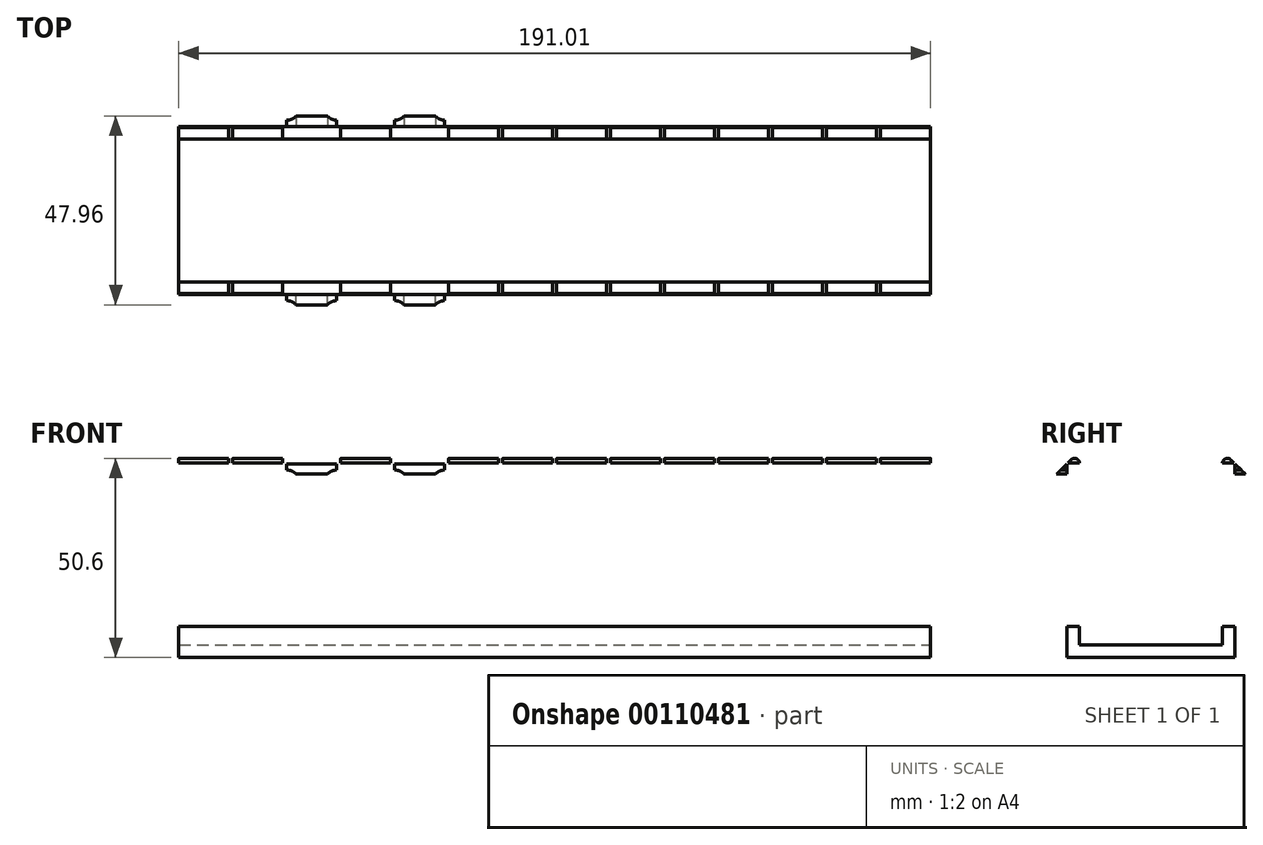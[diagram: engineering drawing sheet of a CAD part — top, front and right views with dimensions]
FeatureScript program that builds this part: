
annotation { "Feature Type Name" : "Feature", "Feature Type Description" : "" }
export const myFeature = defineFeature(function(context is Context, id is Id, definition is map)
    precondition{}
    {
        {
            var Q0;
            Q0=qCreatedBy(makeId("Right.planeOp"),FACE);
            var sketch = newSketch(context, id + "F0", { "sketchPlane" : qUnion([Q0])});
            skLineSegment(sketch, "E0.bottom", {"start": v(21.34, 1.59) * mm, "end": v(-21.34, 1.59) * mm});
            skLineSegment(sketch, "E0.top", {"start": v(21.34, -1.59) * mm, "end": v(-21.34, -1.59) * mm});
            skLineSegment(sketch, "E0.left", {"start": v(21.34, 1.59) * mm, "end": v(21.34, -1.59) * mm});
            skLineSegment(sketch, "E0.right", {"start": v(-21.34, 1.59) * mm, "end": v(-21.34, -1.59) * mm});
            skPoint(sketch, "E0.middle", {"position": v(0, 0) * mm});
            skSolve(sketch);
        }
        {
            var Q0;
            Q0 = qSketchRegion(id + "F0", true);
            extrude(context, id + "F1", {"entities" : qUnion([Q0]), "oppositeDirection" : true, "depth" : 191 * mm});
        }
        {
            var Q0;
            Q0=makeQuery(id+"F1.opExtrude","SWEPT_FACE",FACE,{"disambiguationData":[OSD([sQuery(id+"F0.wireOp",EDGE,"E0.bottom")])]});
            var sketch = newSketch(context, id + "F2", { "sketchPlane" : qUnion([Q0])});
            skLineSegment(sketch, "E1", {"start": v(-191, 18.16) * mm, "end": v(0, 18.16) * mm});
            skLineSegment(sketch, "E2", {"start": v(0, -18.16) * mm, "end": v(-191, -18.16) * mm});
            skSolve(sketch);
        }
        {
            var Q0;
            Q0 = qSketchRegion(id + "F2", true);
            var Q1;
            {var subQ0=sQuery(id+"F2.wireOp",EDGE,"E1");Q1=makeQuery(id+"F2.imprint","IMPRINT",FACE,{"disambiguationData":[TD([[makeQuery(id+"F2.imprint","IMPRINT",EDGE,{"derivedFrom":subQ0}),1.0]])]});}
            var Q2;
            {var subQ0=sQuery(id+"F2.wireOp",EDGE,"E2");Q2=makeQuery(id+"F2.imprint","IMPRINT",FACE,{"disambiguationData":[TD([[makeQuery(id+"F2.imprint","IMPRINT",EDGE,{"derivedFrom":subQ0}),1.0]])]});}
            extrude(context, id + "F3", {"entities" : qUnion([Q0, Q1, Q2]), "operationType" : NewBodyOperationType.ADD, "depth" : 4.7 * mm});
        }
        {
            var Q0;
            {var subQ0=sQuery(id+"F0.wireOp",EDGE,"E0.right");Q0=makeQuery(id+"F3.boolean.opBoolean","MERGE",FACE,{"derivedFrom":[makeQuery(id+"F1.opExtrude","SWEPT_FACE",FACE,{"disambiguationData":[OSD([subQ0])]}),makeQuery(id+"F3.opExtrude","SWEPT_FACE",FACE,{"disambiguationData":[OSD([sQuery(id+"F0.wireOp",EDGE,"E0.bottom"),subQ0])]})]});}
            var sketch = newSketch(context, id + "F4", { "sketchPlane" : qUnion([Q0])});
            skLineSegment(sketch, "E3", {"start": v(-9.53, 11.37) * mm, "end": v(-9.53, 42.86) * mm});
            skLineSegment(sketch, "E4", {"start": v(-3.18, 11.37) * mm, "end": v(-3.18, 42.86) * mm});
            skPoint(sketch, "E5.visualSharp", {"position": v(-3.18, 5.02) * mm});
            skArc(sketch, "E5.filletArc", {"start": v(-3.18, 11.37) * mm, "mid": v(-2.25, 9.12) * mm, "end": v(0, 8.2) * mm});
            skPoint(sketch, "E6.visualSharp", {"position": v(-9.53, 5.06) * mm});
            skArc(sketch, "E6.filletArc", {"start": v(-12.7, 8.2) * mm, "mid": v(-10.45, 9.12) * mm, "end": v(-9.53, 11.37) * mm});
            skArc(sketch, "E7", {"start": v(-3.18, 42.86) * mm, "mid": v(-2.25, 45.1) * mm, "end": v(0, 46.04) * mm});
            skArc(sketch, "E8", {"start": v(-9.53, 42.86) * mm, "mid": v(-10.45, 45.1) * mm, "end": v(-12.7, 46.04) * mm});
            skLineSegment(sketch, "E9", {"start": v(-12.7, 46.04) * mm, "end": v(-12.7, 49.21) * mm});
            skLineSegment(sketch, "E10", {"start": v(-12.7, 49.21) * mm, "end": v(0, 49.21) * mm});
            skLineSegment(sketch, "E11", {"start": v(0, 49.21) * mm, "end": v(0, 46.04) * mm});
            skLineSegment(sketch, "E12", {"start": v(0, 8.2) * mm, "end": v(0, 6.29) * mm});
            skLineSegment(sketch, "E13", {"start": v(-12.7, 8.2) * mm, "end": v(-12.7, 6.29) * mm});
            skLineSegment(sketch, "E14", {"start": v(-12.7, 6.29) * mm, "end": v(0, 6.29) * mm});
            skLineSegment(sketch, "E15", {"start": v(-6.35, 49.21) * mm, "end": v(-6.35, 6.29) * mm, "construction": true});
            skLineSegment(sketch, "E16.1.0.0", {"start": v(-23.24, 11.37) * mm, "end": v(-23.24, 42.86) * mm});
            skArc(sketch, "E16.1.0.1", {"start": v(-16.9, 42.86) * mm, "mid": v(-15.96, 45.1) * mm, "end": v(-13.72, 46.04) * mm});
            skArc(sketch, "E16.1.0.2", {"start": v(-26.42, 8.2) * mm, "mid": v(-24.17, 9.12) * mm, "end": v(-23.24, 11.37) * mm});
            skLineSegment(sketch, "E16.1.0.3", {"start": v(-20.07, 49.21) * mm, "end": v(-20.07, 6.29) * mm, "construction": true});
            skArc(sketch, "E16.1.0.4", {"start": v(-16.9, 11.37) * mm, "mid": v(-15.96, 9.12) * mm, "end": v(-13.72, 8.2) * mm});
            skLineSegment(sketch, "E16.1.0.5", {"start": v(-16.9, 11.37) * mm, "end": v(-16.9, 42.86) * mm});
            skArc(sketch, "E16.1.0.6", {"start": v(-23.24, 42.86) * mm, "mid": v(-24.17, 45.1) * mm, "end": v(-26.42, 46.04) * mm});
            skLineSegment(sketch, "E16.1.0.7", {"start": v(-13.72, 49.21) * mm, "end": v(-13.72, 46.04) * mm});
            skLineSegment(sketch, "E16.1.0.8", {"start": v(-26.42, 46.04) * mm, "end": v(-26.42, 49.21) * mm});
            skLineSegment(sketch, "E16.1.0.9", {"start": v(-26.42, 49.21) * mm, "end": v(-13.72, 49.21) * mm});
            skLineSegment(sketch, "E16.1.0.10", {"start": v(-26.42, 8.2) * mm, "end": v(-26.42, 6.29) * mm});
            skLineSegment(sketch, "E16.1.0.11", {"start": v(-13.72, 8.2) * mm, "end": v(-13.72, 6.29) * mm});
            skLineSegment(sketch, "E16.2.0.0", {"start": v(-36.96, 11.37) * mm, "end": v(-36.96, 42.86) * mm});
            skArc(sketch, "E16.2.0.1", {"start": v(-30.6, 42.86) * mm, "mid": v(-29.68, 45.1) * mm, "end": v(-27.43, 46.04) * mm});
            skArc(sketch, "E16.2.0.2", {"start": v(-40.13, 8.2) * mm, "mid": v(-37.89, 9.12) * mm, "end": v(-36.96, 11.37) * mm});
            skLineSegment(sketch, "E16.2.0.3", {"start": v(-33.78, 49.21) * mm, "end": v(-33.78, 6.29) * mm, "construction": true});
            skArc(sketch, "E16.2.0.4", {"start": v(-30.6, 11.37) * mm, "mid": v(-29.68, 9.12) * mm, "end": v(-27.43, 8.2) * mm});
            skLineSegment(sketch, "E16.2.0.5", {"start": v(-30.6, 11.37) * mm, "end": v(-30.6, 42.86) * mm});
            skArc(sketch, "E16.2.0.6", {"start": v(-36.96, 42.86) * mm, "mid": v(-37.89, 45.1) * mm, "end": v(-40.13, 46.04) * mm});
            skLineSegment(sketch, "E16.2.0.7", {"start": v(-27.43, 49.21) * mm, "end": v(-27.43, 46.04) * mm});
            skLineSegment(sketch, "E16.2.0.8", {"start": v(-40.13, 46.04) * mm, "end": v(-40.13, 49.21) * mm});
            skLineSegment(sketch, "E16.2.0.9", {"start": v(-40.13, 49.21) * mm, "end": v(-27.43, 49.21) * mm});
            skLineSegment(sketch, "E16.2.0.10", {"start": v(-40.13, 8.2) * mm, "end": v(-40.13, 6.29) * mm});
            skLineSegment(sketch, "E16.2.0.11", {"start": v(-27.43, 8.2) * mm, "end": v(-27.43, 6.29) * mm});
            skLineSegment(sketch, "E16.direction1", {"start": v(-12.7, 6.29) * mm, "end": v(-26.42, 6.29) * mm, "construction": true});
            skArc(sketch, "E17.1.0.0", {"start": v(-53.85, 8.2) * mm, "mid": v(-51.6, 9.12) * mm, "end": v(-50.67, 11.37) * mm});
            skLineSegment(sketch, "E17.1.0.1", {"start": v(-81.28, 46.04) * mm, "end": v(-81.28, 49.21) * mm});
            skLineSegment(sketch, "E17.1.0.2", {"start": v(-71.76, 11.37) * mm, "end": v(-71.76, 42.86) * mm});
            skArc(sketch, "E17.1.0.3", {"start": v(-58.04, 11.37) * mm, "mid": v(-57.1, 9.12) * mm, "end": v(-54.86, 8.2) * mm});
            skArc(sketch, "E17.1.0.4", {"start": v(-67.56, 8.2) * mm, "mid": v(-65.32, 9.12) * mm, "end": v(-64.39, 11.37) * mm});
            skArc(sketch, "E17.1.0.5", {"start": v(-81.28, 8.2) * mm, "mid": v(-79.03, 9.12) * mm, "end": v(-78.1, 11.37) * mm});
            skLineSegment(sketch, "E17.1.0.6", {"start": v(-78.1, 11.37) * mm, "end": v(-78.1, 42.86) * mm});
            skLineSegment(sketch, "E17.1.0.7", {"start": v(-53.85, 49.21) * mm, "end": v(-41.15, 49.21) * mm});
            skLineSegment(sketch, "E17.1.0.8", {"start": v(-41.15, 49.21) * mm, "end": v(-41.15, 46.04) * mm});
            skLineSegment(sketch, "E17.1.0.9", {"start": v(-54.86, 49.21) * mm, "end": v(-54.86, 46.04) * mm});
            skArc(sketch, "E17.1.0.10", {"start": v(-44.32, 11.37) * mm, "mid": v(-43.4, 9.12) * mm, "end": v(-41.15, 8.2) * mm});
            skArc(sketch, "E17.1.0.11", {"start": v(-71.75, 11.37) * mm, "mid": v(-70.83, 9.12) * mm, "end": v(-68.58, 8.2) * mm});
            skLineSegment(sketch, "E17.1.0.12", {"start": v(-44.32, 11.37) * mm, "end": v(-44.32, 42.86) * mm});
            skArc(sketch, "E17.1.0.13", {"start": v(-78.1, 42.86) * mm, "mid": v(-79.03, 45.1) * mm, "end": v(-81.28, 46.04) * mm});
            skArc(sketch, "E17.1.0.14", {"start": v(-44.32, 42.86) * mm, "mid": v(-43.4, 45.1) * mm, "end": v(-41.15, 46.04) * mm});
            skLineSegment(sketch, "E17.1.0.15", {"start": v(-53.85, 46.04) * mm, "end": v(-53.85, 49.21) * mm});
            skLineSegment(sketch, "E17.1.0.16", {"start": v(-68.58, 49.21) * mm, "end": v(-68.58, 46.04) * mm});
            skLineSegment(sketch, "E17.1.0.17", {"start": v(-50.67, 11.37) * mm, "end": v(-50.67, 42.86) * mm});
            skLineSegment(sketch, "E17.1.0.18", {"start": v(-64.39, 11.37) * mm, "end": v(-64.39, 42.86) * mm});
            skLineSegment(sketch, "E17.1.0.19", {"start": v(-67.56, 46.04) * mm, "end": v(-67.56, 49.21) * mm});
            skArc(sketch, "E17.1.0.20", {"start": v(-50.67, 42.86) * mm, "mid": v(-51.6, 45.1) * mm, "end": v(-53.85, 46.04) * mm});
            skLineSegment(sketch, "E17.1.0.21", {"start": v(-81.28, 49.21) * mm, "end": v(-68.58, 49.21) * mm});
            skLineSegment(sketch, "E17.1.0.22", {"start": v(-58.04, 11.37) * mm, "end": v(-58.04, 42.86) * mm});
            skArc(sketch, "E17.1.0.23", {"start": v(-71.76, 42.86) * mm, "mid": v(-70.83, 45.1) * mm, "end": v(-68.58, 46.04) * mm});
            skLineSegment(sketch, "E17.1.0.24", {"start": v(-67.56, 49.21) * mm, "end": v(-54.86, 49.21) * mm});
            skArc(sketch, "E17.1.0.25", {"start": v(-58.04, 42.86) * mm, "mid": v(-57.1, 45.1) * mm, "end": v(-54.86, 46.04) * mm});
            skArc(sketch, "E17.1.0.26", {"start": v(-64.39, 42.86) * mm, "mid": v(-65.32, 45.1) * mm, "end": v(-67.56, 46.04) * mm});
            skLineSegment(sketch, "E17.1.0.27", {"start": v(-41.15, 8.2) * mm, "end": v(-41.15, 6.29) * mm});
            skLineSegment(sketch, "E17.1.0.28", {"start": v(-53.85, 8.2) * mm, "end": v(-53.85, 6.29) * mm});
            skLineSegment(sketch, "E17.1.0.29", {"start": v(-54.86, 8.2) * mm, "end": v(-54.86, 6.29) * mm});
            skLineSegment(sketch, "E17.1.0.30", {"start": v(-67.56, 8.2) * mm, "end": v(-67.56, 6.29) * mm});
            skLineSegment(sketch, "E17.1.0.31", {"start": v(-68.58, 8.2) * mm, "end": v(-68.58, 6.29) * mm});
            skLineSegment(sketch, "E17.1.0.32", {"start": v(-81.28, 8.2) * mm, "end": v(-81.28, 6.29) * mm});
            skArc(sketch, "E17.2.0.0", {"start": v(-95, 8.2) * mm, "mid": v(-92.75, 9.12) * mm, "end": v(-91.82, 11.37) * mm});
            skLineSegment(sketch, "E17.2.0.1", {"start": v(-122.43, 46.04) * mm, "end": v(-122.43, 49.21) * mm});
            skLineSegment(sketch, "E17.2.0.2", {"start": v(-112.9, 11.37) * mm, "end": v(-112.9, 42.86) * mm});
            skArc(sketch, "E17.2.0.3", {"start": v(-99.19, 11.37) * mm, "mid": v(-98.26, 9.12) * mm, "end": v(-96.01, 8.2) * mm});
            skArc(sketch, "E17.2.0.4", {"start": v(-108.71, 8.2) * mm, "mid": v(-106.47, 9.12) * mm, "end": v(-105.54, 11.37) * mm});
            skArc(sketch, "E17.2.0.5", {"start": v(-122.43, 8.2) * mm, "mid": v(-120.18, 9.12) * mm, "end": v(-119.25, 11.37) * mm});
            skLineSegment(sketch, "E17.2.0.6", {"start": v(-119.25, 11.37) * mm, "end": v(-119.25, 42.86) * mm});
            skLineSegment(sketch, "E17.2.0.7", {"start": v(-95, 49.21) * mm, "end": v(-82.3, 49.21) * mm});
            skLineSegment(sketch, "E17.2.0.8", {"start": v(-82.3, 49.21) * mm, "end": v(-82.3, 46.04) * mm});
            skLineSegment(sketch, "E17.2.0.9", {"start": v(-96.01, 49.21) * mm, "end": v(-96.01, 46.04) * mm});
            skArc(sketch, "E17.2.0.10", {"start": v(-85.47, 11.37) * mm, "mid": v(-84.54, 9.12) * mm, "end": v(-82.3, 8.2) * mm});
            skArc(sketch, "E17.2.0.11", {"start": v(-112.9, 11.37) * mm, "mid": v(-111.97, 9.12) * mm, "end": v(-109.73, 8.2) * mm});
            skLineSegment(sketch, "E17.2.0.12", {"start": v(-85.47, 11.37) * mm, "end": v(-85.47, 42.86) * mm});
            skArc(sketch, "E17.2.0.13", {"start": v(-119.25, 42.86) * mm, "mid": v(-120.18, 45.1) * mm, "end": v(-122.43, 46.04) * mm});
            skArc(sketch, "E17.2.0.14", {"start": v(-85.47, 42.86) * mm, "mid": v(-84.54, 45.1) * mm, "end": v(-82.3, 46.04) * mm});
            skLineSegment(sketch, "E17.2.0.15", {"start": v(-95, 46.04) * mm, "end": v(-95, 49.21) * mm});
            skLineSegment(sketch, "E17.2.0.16", {"start": v(-109.73, 49.21) * mm, "end": v(-109.73, 46.04) * mm});
            skLineSegment(sketch, "E17.2.0.17", {"start": v(-91.82, 11.37) * mm, "end": v(-91.82, 42.86) * mm});
            skLineSegment(sketch, "E17.2.0.18", {"start": v(-105.54, 11.37) * mm, "end": v(-105.54, 42.86) * mm});
            skLineSegment(sketch, "E17.2.0.19", {"start": v(-108.71, 46.04) * mm, "end": v(-108.71, 49.21) * mm});
            skArc(sketch, "E17.2.0.20", {"start": v(-91.82, 42.86) * mm, "mid": v(-92.75, 45.1) * mm, "end": v(-95, 46.04) * mm});
            skLineSegment(sketch, "E17.2.0.21", {"start": v(-122.43, 49.21) * mm, "end": v(-109.73, 49.21) * mm});
            skLineSegment(sketch, "E17.2.0.22", {"start": v(-99.19, 11.37) * mm, "end": v(-99.19, 42.86) * mm});
            skArc(sketch, "E17.2.0.23", {"start": v(-112.9, 42.86) * mm, "mid": v(-111.97, 45.1) * mm, "end": v(-109.73, 46.04) * mm});
            skLineSegment(sketch, "E17.2.0.24", {"start": v(-108.71, 49.21) * mm, "end": v(-96.01, 49.21) * mm});
            skArc(sketch, "E17.2.0.25", {"start": v(-99.19, 42.86) * mm, "mid": v(-98.26, 45.1) * mm, "end": v(-96.01, 46.04) * mm});
            skArc(sketch, "E17.2.0.26", {"start": v(-105.54, 42.86) * mm, "mid": v(-106.47, 45.1) * mm, "end": v(-108.71, 46.04) * mm});
            skLineSegment(sketch, "E17.2.0.27", {"start": v(-82.3, 8.2) * mm, "end": v(-82.3, 6.29) * mm});
            skLineSegment(sketch, "E17.2.0.28", {"start": v(-95, 8.2) * mm, "end": v(-95, 6.29) * mm});
            skLineSegment(sketch, "E17.2.0.29", {"start": v(-96.01, 8.2) * mm, "end": v(-96.01, 6.29) * mm});
            skLineSegment(sketch, "E17.2.0.30", {"start": v(-108.71, 8.2) * mm, "end": v(-108.71, 6.29) * mm});
            skLineSegment(sketch, "E17.2.0.31", {"start": v(-109.73, 8.2) * mm, "end": v(-109.73, 6.29) * mm});
            skLineSegment(sketch, "E17.2.0.32", {"start": v(-122.43, 8.2) * mm, "end": v(-122.43, 6.29) * mm});
            skLineSegment(sketch, "E17.direction1", {"start": v(-40.13, 8.2) * mm, "end": v(-81.28, 8.2) * mm, "construction": true});
            skArc(sketch, "E18.1.0.0", {"start": v(-126.62, 42.86) * mm, "mid": v(-125.69, 45.1) * mm, "end": v(-123.44, 46.04) * mm});
            skLineSegment(sketch, "E18.1.0.1", {"start": v(-146.69, 11.37) * mm, "end": v(-146.69, 42.86) * mm});
            skLineSegment(sketch, "E18.1.0.2", {"start": v(-126.62, 11.37) * mm, "end": v(-126.62, 42.86) * mm});
            skArc(sketch, "E18.1.0.3", {"start": v(-136.14, 8.2) * mm, "mid": v(-133.9, 9.12) * mm, "end": v(-132.97, 11.37) * mm});
            skArc(sketch, "E18.1.0.4", {"start": v(-126.62, 11.37) * mm, "mid": v(-125.69, 9.12) * mm, "end": v(-123.44, 8.2) * mm});
            skLineSegment(sketch, "E18.1.0.5", {"start": v(-132.97, 11.37) * mm, "end": v(-132.97, 42.86) * mm});
            skLineSegment(sketch, "E18.1.0.6", {"start": v(-140.34, 11.37) * mm, "end": v(-140.34, 42.86) * mm});
            skLineSegment(sketch, "E18.1.0.7", {"start": v(-149.86, 49.21) * mm, "end": v(-137.16, 49.21) * mm});
            skLineSegment(sketch, "E18.1.0.8", {"start": v(-136.14, 49.21) * mm, "end": v(-123.44, 49.21) * mm});
            skArc(sketch, "E18.1.0.9", {"start": v(-149.86, 8.2) * mm, "mid": v(-147.61, 9.12) * mm, "end": v(-146.69, 11.37) * mm});
            skArc(sketch, "E18.1.0.10", {"start": v(-132.97, 42.86) * mm, "mid": v(-133.9, 45.1) * mm, "end": v(-136.14, 46.04) * mm});
            skArc(sketch, "E18.1.0.11", {"start": v(-140.34, 11.37) * mm, "mid": v(-139.4, 9.12) * mm, "end": v(-137.16, 8.2) * mm});
            skArc(sketch, "E18.1.0.12", {"start": v(-146.69, 42.86) * mm, "mid": v(-147.61, 45.1) * mm, "end": v(-149.86, 46.04) * mm});
            skArc(sketch, "E18.1.0.13", {"start": v(-140.34, 42.86) * mm, "mid": v(-139.4, 45.1) * mm, "end": v(-137.16, 46.04) * mm});
            skLineSegment(sketch, "E18.1.0.14", {"start": v(-123.44, 49.21) * mm, "end": v(-123.44, 46.04) * mm});
            skLineSegment(sketch, "E18.1.0.15", {"start": v(-136.14, 46.04) * mm, "end": v(-136.14, 49.21) * mm});
            skLineSegment(sketch, "E18.1.0.16", {"start": v(-149.86, 46.04) * mm, "end": v(-149.86, 49.21) * mm});
            skLineSegment(sketch, "E18.1.0.17", {"start": v(-137.16, 49.21) * mm, "end": v(-137.16, 46.04) * mm});
            skLineSegment(sketch, "E18.1.0.18", {"start": v(-136.14, 8.2) * mm, "end": v(-136.14, 6.29) * mm});
            skLineSegment(sketch, "E18.1.0.19", {"start": v(-137.16, 8.2) * mm, "end": v(-137.16, 6.29) * mm});
            skLineSegment(sketch, "E18.1.0.20", {"start": v(-149.86, 8.2) * mm, "end": v(-149.86, 6.29) * mm});
            skLineSegment(sketch, "E18.1.0.21", {"start": v(-123.44, 8.2) * mm, "end": v(-123.44, 6.29) * mm});
            skArc(sketch, "E18.2.0.0", {"start": v(-154.05, 42.86) * mm, "mid": v(-153.12, 45.1) * mm, "end": v(-150.88, 46.04) * mm});
            skLineSegment(sketch, "E18.2.0.1", {"start": v(-174.12, 11.37) * mm, "end": v(-174.12, 42.86) * mm});
            skLineSegment(sketch, "E18.2.0.2", {"start": v(-154.05, 11.37) * mm, "end": v(-154.05, 42.86) * mm});
            skArc(sketch, "E18.2.0.3", {"start": v(-163.58, 8.2) * mm, "mid": v(-161.33, 9.12) * mm, "end": v(-160.4, 11.37) * mm});
            skArc(sketch, "E18.2.0.4", {"start": v(-154.05, 11.37) * mm, "mid": v(-153.12, 9.12) * mm, "end": v(-150.88, 8.2) * mm});
            skLineSegment(sketch, "E18.2.0.5", {"start": v(-160.4, 11.37) * mm, "end": v(-160.4, 42.86) * mm});
            skLineSegment(sketch, "E18.2.0.6", {"start": v(-167.77, 11.37) * mm, "end": v(-167.77, 42.86) * mm});
            skLineSegment(sketch, "E18.2.0.7", {"start": v(-177.3, 49.21) * mm, "end": v(-164.6, 49.21) * mm});
            skLineSegment(sketch, "E18.2.0.8", {"start": v(-163.58, 49.21) * mm, "end": v(-150.88, 49.21) * mm});
            skArc(sketch, "E18.2.0.9", {"start": v(-177.3, 8.2) * mm, "mid": v(-175.05, 9.12) * mm, "end": v(-174.12, 11.37) * mm});
            skArc(sketch, "E18.2.0.10", {"start": v(-160.4, 42.86) * mm, "mid": v(-161.33, 45.1) * mm, "end": v(-163.58, 46.04) * mm});
            skArc(sketch, "E18.2.0.11", {"start": v(-167.77, 11.37) * mm, "mid": v(-166.84, 9.12) * mm, "end": v(-164.6, 8.2) * mm});
            skArc(sketch, "E18.2.0.12", {"start": v(-174.12, 42.86) * mm, "mid": v(-175.05, 45.1) * mm, "end": v(-177.3, 46.04) * mm});
            skArc(sketch, "E18.2.0.13", {"start": v(-167.77, 42.86) * mm, "mid": v(-166.84, 45.1) * mm, "end": v(-164.6, 46.04) * mm});
            skLineSegment(sketch, "E18.2.0.14", {"start": v(-150.88, 49.21) * mm, "end": v(-150.88, 46.04) * mm});
            skLineSegment(sketch, "E18.2.0.15", {"start": v(-163.58, 46.04) * mm, "end": v(-163.58, 49.21) * mm});
            skLineSegment(sketch, "E18.2.0.16", {"start": v(-177.3, 46.04) * mm, "end": v(-177.3, 49.21) * mm});
            skLineSegment(sketch, "E18.2.0.17", {"start": v(-164.6, 49.21) * mm, "end": v(-164.6, 46.04) * mm});
            skLineSegment(sketch, "E18.2.0.18", {"start": v(-163.58, 8.2) * mm, "end": v(-163.58, 6.29) * mm});
            skLineSegment(sketch, "E18.2.0.19", {"start": v(-164.6, 8.2) * mm, "end": v(-164.6, 6.29) * mm});
            skLineSegment(sketch, "E18.2.0.20", {"start": v(-177.3, 8.2) * mm, "end": v(-177.3, 6.29) * mm});
            skLineSegment(sketch, "E18.2.0.21", {"start": v(-150.88, 8.2) * mm, "end": v(-150.88, 6.29) * mm});
            skLineSegment(sketch, "E18.direction1", {"start": v(-122.43, 8.2) * mm, "end": v(-149.86, 8.2) * mm, "construction": true});
            skArc(sketch, "E19.1.0.0", {"start": v(-191, 8.2) * mm, "mid": v(-188.76, 9.12) * mm, "end": v(-187.83, 11.37) * mm});
            skLineSegment(sketch, "E19.1.0.1", {"start": v(-191, 49.21) * mm, "end": v(-178.3, 49.21) * mm});
            skLineSegment(sketch, "E19.1.0.2", {"start": v(-181.48, 11.37) * mm, "end": v(-181.48, 42.86) * mm});
            skArc(sketch, "E19.1.0.3", {"start": v(-187.83, 42.86) * mm, "mid": v(-188.76, 45.1) * mm, "end": v(-191, 46.04) * mm});
            skArc(sketch, "E19.1.0.4", {"start": v(-181.48, 11.37) * mm, "mid": v(-180.55, 9.12) * mm, "end": v(-178.3, 8.2) * mm});
            skLineSegment(sketch, "E19.1.0.5", {"start": v(-187.83, 11.37) * mm, "end": v(-187.83, 42.86) * mm});
            skArc(sketch, "E19.1.0.6", {"start": v(-181.48, 42.86) * mm, "mid": v(-180.55, 45.1) * mm, "end": v(-178.3, 46.04) * mm});
            skLineSegment(sketch, "E19.1.0.7", {"start": v(-178.3, 49.21) * mm, "end": v(-178.3, 46.04) * mm});
            skLineSegment(sketch, "E19.1.0.8", {"start": v(-191, 46.04) * mm, "end": v(-191, 49.21) * mm});
            skLineSegment(sketch, "E19.1.0.9", {"start": v(-178.3, 8.2) * mm, "end": v(-178.3, 6.29) * mm});
            skLineSegment(sketch, "E19.1.0.10", {"start": v(-191, 8.2) * mm, "end": v(-191, 6.29) * mm});
            skLineSegment(sketch, "E19.direction1", {"start": v(-177.3, 6.29) * mm, "end": v(-191, 6.29) * mm, "construction": true});
            skSolve(sketch);
        }
        {
            var Q0;
            Q0 = qSketchRegion(id + "F4", true);
            var Q1;
            Q1=makeQuery(id+"F4.imprint","IMPRINT",FACE,{"disambiguationData":[TD([[makeQuery(id+"F4.imprint","IMPRINT",EDGE,{"derivedFrom":sQuery(id+"F4.wireOp",EDGE,"E16.1.0.0")}),-1.0]])]});
            var Q2;
            Q2=makeQuery(id+"F4.imprint","IMPRINT",FACE,{"disambiguationData":[TD([[makeQuery(id+"F4.imprint","IMPRINT",EDGE,{"derivedFrom":sQuery(id+"F4.wireOp",EDGE,"E16.2.0.0")}),-1.0]])]});
            var Q3;
            Q3=makeQuery(id+"F4.imprint","IMPRINT",FACE,{"disambiguationData":[TD([[makeQuery(id+"F4.imprint","IMPRINT",EDGE,{"derivedFrom":sQuery(id+"F4.wireOp",EDGE,"E17.1.0.0")}),-1.0]])]});
            var Q4;
            Q4=makeQuery(id+"F4.imprint","IMPRINT",FACE,{"disambiguationData":[TD([[makeQuery(id+"F4.imprint","IMPRINT",EDGE,{"derivedFrom":sQuery(id+"F4.wireOp",EDGE,"E17.1.0.3")}),-1.0]])]});
            var Q5;
            Q5=makeQuery(id+"F4.imprint","IMPRINT",FACE,{"disambiguationData":[TD([[makeQuery(id+"F4.imprint","IMPRINT",EDGE,{"derivedFrom":sQuery(id+"F4.wireOp",EDGE,"E17.1.0.1")}),-1.0]])]});
            var Q6;
            Q6=makeQuery(id+"F4.imprint","IMPRINT",FACE,{"disambiguationData":[TD([[makeQuery(id+"F4.imprint","IMPRINT",EDGE,{"derivedFrom":sQuery(id+"F4.wireOp",EDGE,"E17.2.0.0")}),-1.0]])]});
            var Q7;
            Q7=makeQuery(id+"F4.imprint","IMPRINT",FACE,{"disambiguationData":[TD([[makeQuery(id+"F4.imprint","IMPRINT",EDGE,{"derivedFrom":sQuery(id+"F4.wireOp",EDGE,"E17.2.0.3")}),-1.0]])]});
            var Q8;
            Q8=makeQuery(id+"F4.imprint","IMPRINT",FACE,{"disambiguationData":[TD([[makeQuery(id+"F4.imprint","IMPRINT",EDGE,{"derivedFrom":sQuery(id+"F4.wireOp",EDGE,"E17.2.0.1")}),-1.0]])]});
            var Q9;
            Q9=makeQuery(id+"F4.imprint","IMPRINT",FACE,{"disambiguationData":[TD([[makeQuery(id+"F4.imprint","IMPRINT",EDGE,{"derivedFrom":sQuery(id+"F4.wireOp",EDGE,"E18.1.0.0")}),1.0]])]});
            var Q10;
            Q10=makeQuery(id+"F4.imprint","IMPRINT",FACE,{"disambiguationData":[TD([[makeQuery(id+"F4.imprint","IMPRINT",EDGE,{"derivedFrom":sQuery(id+"F4.wireOp",EDGE,"E18.1.0.1")}),-1.0]])]});
            var Q11;
            Q11=makeQuery(id+"F4.imprint","IMPRINT",FACE,{"disambiguationData":[TD([[makeQuery(id+"F4.imprint","IMPRINT",EDGE,{"derivedFrom":sQuery(id+"F4.wireOp",EDGE,"E18.2.0.0")}),1.0]])]});
            var Q12;
            Q12=makeQuery(id+"F4.imprint","IMPRINT",FACE,{"disambiguationData":[TD([[makeQuery(id+"F4.imprint","IMPRINT",EDGE,{"derivedFrom":sQuery(id+"F4.wireOp",EDGE,"E18.2.0.1")}),-1.0]])]});
            var Q13;
            Q13=makeQuery(id+"F4.imprint","IMPRINT",FACE,{"disambiguationData":[TD([[makeQuery(id+"F4.imprint","IMPRINT",EDGE,{"derivedFrom":sQuery(id+"F4.wireOp",EDGE,"E19.1.0.0")}),-1.0]])]});
            extrude(context, id + "F5", {"entities" : qUnion([Q0, Q1, Q2, Q3, Q4, Q5, Q6, Q7, Q8, Q9, Q10, Q11, Q12, Q13]), "operationType" : NewBodyOperationType.ADD, "oppositeDirection" : true, "depth" : 3.17 * mm});
        }
        {
            var Q0;
            Q0=makeQuery(id+"F5.opExtrude","SWEPT_FACE",FACE,{"disambiguationData":[OSD([sQuery(id+"F4.wireOp",EDGE,"E11")])]});
            var sketch = newSketch(context, id + "F6", { "sketchPlane" : qUnion([Q0])});
            skLineSegment(sketch, "E20", {"start": v(-23.98, 44.98) * mm, "end": v(-21.34, 44.98) * mm});
            skArc(sketch, "E21", {"start": v(-20.32, 48.64) * mm, "mid": v(-18.89, 48.89) * mm, "end": v(-18.16, 47.62) * mm});
            skLineSegment(sketch, "E22", {"start": v(-23.98, 44.98) * mm, "end": v(-20.32, 48.64) * mm});
            skLineSegment(sketch, "E23", {"start": v(-21.34, 44.98) * mm, "end": v(-21.34, 47.62) * mm});
            skLineSegment(sketch, "E24", {"start": v(-21.34, 47.62) * mm, "end": v(-18.16, 47.62) * mm});
            skSolve(sketch);
        }
        {
            var Q0;
            {var subQ0=sQuery(id+"F6.wireOp",EDGE,"E20");Q0=makeQuery(id+"F6.imprint","IMPRINT",FACE,{"disambiguationData":[TD([[makeQuery(id+"F6.imprint","IMPRINT",EDGE,{"derivedFrom":subQ0}),1.0]])]});}
            extrude(context, id + "F7", {"entities" : qUnion([Q0]), "operationType" : NewBodyOperationType.ADD, "oppositeDirection" : true, "depth" : 191 * mm});
        }
        {
            var Q0;
            {var subQ0=sQuery(id+"F4.wireOp",EDGE,"E11");var subQ1=makeQuery(id+"F5.opExtrude","SWEPT_EDGE",EDGE,{"disambiguationData":[OSD([sQuery(id+"F4.wireOp",EDGE,"E10"),subQ0])]});Q0=makeQuery(id+"F6.imprint","IMPRINT",FACE,{"disambiguationData":[TD([[makeQuery(id+"F6.imprint","IMPRINT",EDGE,{"derivedFrom":subQ1}),1.0]])]});}
            extrude(context, id + "F8", {"entities" : qUnion([Q0]), "operationType" : NewBodyOperationType.REMOVE, "endBound" : BoundingType.THROUGH_ALL, "oppositeDirection" : true, "depth" : 25.4 * mm});
        }
        {
            var Q0;
            Q0=makeQuery(id+"F5.boolean.opBoolean","MERGE",FACE,{"derivedFrom":[makeQuery(id+"F3.opExtrude","SWEPT_FACE",FACE,{"disambiguationData":[OSD([sQuery(id+"F2.wireOp",EDGE,"E2")])]}),makeQuery(id+"F5.opExtrude","CAP_FACE",FACE,{"disambiguationData":[OSD([sQuery(id+"F4.wireOp",EDGE,"E3"),sQuery(id+"F4.wireOp",EDGE,"E4"),sQuery(id+"F4.wireOp",EDGE,"E5.filletArc"),sQuery(id+"F4.wireOp",EDGE,"E6.filletArc"),sQuery(id+"F4.wireOp",EDGE,"E7"),sQuery(id+"F4.wireOp",EDGE,"E8"),sQuery(id+"F4.wireOp",EDGE,"E9"),sQuery(id+"F4.wireOp",EDGE,"E10"),sQuery(id+"F4.wireOp",EDGE,"E11"),sQuery(id+"F4.wireOp",EDGE,"E12"),sQuery(id+"F4.wireOp",EDGE,"E13"),sQuery(id+"F4.wireOp",EDGE,"E14")])],"isStart":false})]});
            var sketch = newSketch(context, id + "F9", { "sketchPlane" : qUnion([Q0])});
            skArc(sketch, "E25.0", {"start": v(3.18, 42.86) * mm, "mid": v(2.25, 45.1) * mm, "end": v(0, 46.04) * mm});
            skArc(sketch, "E26.0", {"start": v(9.53, 42.86) * mm, "mid": v(10.45, 45.1) * mm, "end": v(12.7, 46.04) * mm});
            skLineSegment(sketch, "E27", {"start": v(0, 46.04) * mm, "end": v(0, 42.86) * mm});
            skLineSegment(sketch, "E28", {"start": v(0, 42.86) * mm, "end": v(3.18, 42.86) * mm});
            skLineSegment(sketch, "E29", {"start": v(9.53, 42.86) * mm, "end": v(12.7, 42.86) * mm});
            skLineSegment(sketch, "E30", {"start": v(12.7, 46.04) * mm, "end": v(12.7, 42.86) * mm});
            skSolve(sketch);
        }
        {
            var Q0;
            Q0 = qSketchRegion(id + "F9", true);
            extrude(context, id + "F10", {"entities" : qUnion([Q0]), "operationType" : NewBodyOperationType.REMOVE, "endBound" : BoundingType.THROUGH_ALL, "oppositeDirection" : true, "depth" : 25.4 * mm});
        }
        {
            var Q0;
            {var subQ0=sQuery(id+"F0.wireOp",EDGE,"E0.right");var subQ1=sQuery(id+"F0.wireOp",EDGE,"E0.bottom");Q0=makeQuery(id+"F5.boolean.opBoolean","MERGE",FACE,{"derivedFrom":[makeQuery(id+"F3.opExtrude","SWEPT_FACE",FACE,{"disambiguationData":[OSD([sQuery(id+"F2.wireOp",EDGE,"E2")])]}),makeQuery(id+"F5.opExtrude","CAP_FACE",FACE,{"disambiguationData":[OSD([sQuery(id+"F4.wireOp",EDGE,"E3"),sQuery(id+"F4.wireOp",EDGE,"E4"),sQuery(id+"F4.wireOp",EDGE,"E5.filletArc"),sQuery(id+"F4.wireOp",EDGE,"E6.filletArc"),sQuery(id+"F4.wireOp",EDGE,"E7"),sQuery(id+"F4.wireOp",EDGE,"E8"),sQuery(id+"F4.wireOp",EDGE,"E9"),sQuery(id+"F4.wireOp",EDGE,"E10"),sQuery(id+"F4.wireOp",EDGE,"E11"),sQuery(id+"F4.wireOp",EDGE,"E12"),sQuery(id+"F4.wireOp",EDGE,"E13"),sQuery(id+"F4.wireOp",EDGE,"E14")])],"isStart":false}),makeQuery(id+"F5.opExtrude","CAP_FACE",FACE,{"disambiguationData":[OSD([subQ1,subQ0,sQuery(id+"F4.wireOp",EDGE,"E16.1.0.0"),sQuery(id+"F4.wireOp",EDGE,"E16.1.0.1"),sQuery(id+"F4.wireOp",EDGE,"E16.1.0.2"),sQuery(id+"F4.wireOp",EDGE,"E16.1.0.4"),sQuery(id+"F4.wireOp",EDGE,"E16.1.0.5"),sQuery(id+"F4.wireOp",EDGE,"E16.1.0.6"),sQuery(id+"F4.wireOp",EDGE,"E16.1.0.7"),sQuery(id+"F4.wireOp",EDGE,"E16.1.0.8"),sQuery(id+"F4.wireOp",EDGE,"E16.1.0.9"),sQuery(id+"F4.wireOp",EDGE,"E16.1.0.10"),sQuery(id+"F4.wireOp",EDGE,"E16.1.0.11")])],"isStart":false}),makeQuery(id+"F5.opExtrude","CAP_FACE",FACE,{"disambiguationData":[OSD([subQ1,subQ0,sQuery(id+"F4.wireOp",EDGE,"E16.2.0.0"),sQuery(id+"F4.wireOp",EDGE,"E16.2.0.1"),sQuery(id+"F4.wireOp",EDGE,"E16.2.0.2"),sQuery(id+"F4.wireOp",EDGE,"E16.2.0.4"),sQuery(id+"F4.wireOp",EDGE,"E16.2.0.5"),sQuery(id+"F4.wireOp",EDGE,"E16.2.0.6"),sQuery(id+"F4.wireOp",EDGE,"E16.2.0.7"),sQuery(id+"F4.wireOp",EDGE,"E16.2.0.8"),sQuery(id+"F4.wireOp",EDGE,"E16.2.0.9"),sQuery(id+"F4.wireOp",EDGE,"E16.2.0.10"),sQuery(id+"F4.wireOp",EDGE,"E16.2.0.11")])],"isStart":false}),makeQuery(id+"F5.opExtrude","CAP_FACE",FACE,{"disambiguationData":[OSD([subQ1,subQ0,sQuery(id+"F4.wireOp",EDGE,"E17.1.0.0"),sQuery(id+"F4.wireOp",EDGE,"E17.1.0.7"),sQuery(id+"F4.wireOp",EDGE,"E17.1.0.8"),sQuery(id+"F4.wireOp",EDGE,"E17.1.0.10"),sQuery(id+"F4.wireOp",EDGE,"E17.1.0.12"),sQuery(id+"F4.wireOp",EDGE,"E17.1.0.14"),sQuery(id+"F4.wireOp",EDGE,"E17.1.0.15"),sQuery(id+"F4.wireOp",EDGE,"E17.1.0.17"),sQuery(id+"F4.wireOp",EDGE,"E17.1.0.20"),sQuery(id+"F4.wireOp",EDGE,"E17.1.0.27"),sQuery(id+"F4.wireOp",EDGE,"E17.1.0.28")])],"isStart":false}),makeQuery(id+"F5.opExtrude","CAP_FACE",FACE,{"disambiguationData":[OSD([subQ1,subQ0,sQuery(id+"F4.wireOp",EDGE,"E17.1.0.1"),sQuery(id+"F4.wireOp",EDGE,"E17.1.0.2"),sQuery(id+"F4.wireOp",EDGE,"E17.1.0.5"),sQuery(id+"F4.wireOp",EDGE,"E17.1.0.6"),sQuery(id+"F4.wireOp",EDGE,"E17.1.0.11"),sQuery(id+"F4.wireOp",EDGE,"E17.1.0.13"),sQuery(id+"F4.wireOp",EDGE,"E17.1.0.16"),sQuery(id+"F4.wireOp",EDGE,"E17.1.0.21"),sQuery(id+"F4.wireOp",EDGE,"E17.1.0.23"),sQuery(id+"F4.wireOp",EDGE,"E17.1.0.31"),sQuery(id+"F4.wireOp",EDGE,"E17.1.0.32")])],"isStart":false}),makeQuery(id+"F5.opExtrude","CAP_FACE",FACE,{"disambiguationData":[OSD([subQ1,subQ0,sQuery(id+"F4.wireOp",EDGE,"E17.1.0.3"),sQuery(id+"F4.wireOp",EDGE,"E17.1.0.4"),sQuery(id+"F4.wireOp",EDGE,"E17.1.0.9"),sQuery(id+"F4.wireOp",EDGE,"E17.1.0.18"),sQuery(id+"F4.wireOp",EDGE,"E17.1.0.19"),sQuery(id+"F4.wireOp",EDGE,"E17.1.0.22"),sQuery(id+"F4.wireOp",EDGE,"E17.1.0.24"),sQuery(id+"F4.wireOp",EDGE,"E17.1.0.25"),sQuery(id+"F4.wireOp",EDGE,"E17.1.0.26"),sQuery(id+"F4.wireOp",EDGE,"E17.1.0.29"),sQuery(id+"F4.wireOp",EDGE,"E17.1.0.30")])],"isStart":false}),makeQuery(id+"F5.opExtrude","CAP_FACE",FACE,{"disambiguationData":[OSD([subQ1,subQ0,sQuery(id+"F4.wireOp",EDGE,"E17.2.0.0"),sQuery(id+"F4.wireOp",EDGE,"E17.2.0.7"),sQuery(id+"F4.wireOp",EDGE,"E17.2.0.8"),sQuery(id+"F4.wireOp",EDGE,"E17.2.0.10"),sQuery(id+"F4.wireOp",EDGE,"E17.2.0.12"),sQuery(id+"F4.wireOp",EDGE,"E17.2.0.14"),sQuery(id+"F4.wireOp",EDGE,"E17.2.0.15"),sQuery(id+"F4.wireOp",EDGE,"E17.2.0.17"),sQuery(id+"F4.wireOp",EDGE,"E17.2.0.20"),sQuery(id+"F4.wireOp",EDGE,"E17.2.0.27"),sQuery(id+"F4.wireOp",EDGE,"E17.2.0.28")])],"isStart":false}),makeQuery(id+"F5.opExtrude","CAP_FACE",FACE,{"disambiguationData":[OSD([subQ1,subQ0,sQuery(id+"F4.wireOp",EDGE,"E17.2.0.1"),sQuery(id+"F4.wireOp",EDGE,"E17.2.0.2"),sQuery(id+"F4.wireOp",EDGE,"E17.2.0.5"),sQuery(id+"F4.wireOp",EDGE,"E17.2.0.6"),sQuery(id+"F4.wireOp",EDGE,"E17.2.0.11"),sQuery(id+"F4.wireOp",EDGE,"E17.2.0.13"),sQuery(id+"F4.wireOp",EDGE,"E17.2.0.16"),sQuery(id+"F4.wireOp",EDGE,"E17.2.0.21"),sQuery(id+"F4.wireOp",EDGE,"E17.2.0.23"),sQuery(id+"F4.wireOp",EDGE,"E17.2.0.31"),sQuery(id+"F4.wireOp",EDGE,"E17.2.0.32")])],"isStart":false}),makeQuery(id+"F5.opExtrude","CAP_FACE",FACE,{"disambiguationData":[OSD([subQ1,subQ0,sQuery(id+"F4.wireOp",EDGE,"E17.2.0.3"),sQuery(id+"F4.wireOp",EDGE,"E17.2.0.4"),sQuery(id+"F4.wireOp",EDGE,"E17.2.0.9"),sQuery(id+"F4.wireOp",EDGE,"E17.2.0.18"),sQuery(id+"F4.wireOp",EDGE,"E17.2.0.19"),sQuery(id+"F4.wireOp",EDGE,"E17.2.0.22"),sQuery(id+"F4.wireOp",EDGE,"E17.2.0.24"),sQuery(id+"F4.wireOp",EDGE,"E17.2.0.25"),sQuery(id+"F4.wireOp",EDGE,"E17.2.0.26"),sQuery(id+"F4.wireOp",EDGE,"E17.2.0.29"),sQuery(id+"F4.wireOp",EDGE,"E17.2.0.30")])],"isStart":false}),makeQuery(id+"F5.opExtrude","CAP_FACE",FACE,{"disambiguationData":[OSD([subQ1,subQ0,sQuery(id+"F4.wireOp",EDGE,"E18.1.0.0"),sQuery(id+"F4.wireOp",EDGE,"E18.1.0.2"),sQuery(id+"F4.wireOp",EDGE,"E18.1.0.3"),sQuery(id+"F4.wireOp",EDGE,"E18.1.0.4"),sQuery(id+"F4.wireOp",EDGE,"E18.1.0.5"),sQuery(id+"F4.wireOp",EDGE,"E18.1.0.8"),sQuery(id+"F4.wireOp",EDGE,"E18.1.0.10"),sQuery(id+"F4.wireOp",EDGE,"E18.1.0.14"),sQuery(id+"F4.wireOp",EDGE,"E18.1.0.15"),sQuery(id+"F4.wireOp",EDGE,"E18.1.0.18"),sQuery(id+"F4.wireOp",EDGE,"E18.1.0.21")])],"isStart":false}),makeQuery(id+"F5.opExtrude","CAP_FACE",FACE,{"disambiguationData":[OSD([subQ1,subQ0,sQuery(id+"F4.wireOp",EDGE,"E18.1.0.1"),sQuery(id+"F4.wireOp",EDGE,"E18.1.0.6"),sQuery(id+"F4.wireOp",EDGE,"E18.1.0.7"),sQuery(id+"F4.wireOp",EDGE,"E18.1.0.9"),sQuery(id+"F4.wireOp",EDGE,"E18.1.0.11"),sQuery(id+"F4.wireOp",EDGE,"E18.1.0.12"),sQuery(id+"F4.wireOp",EDGE,"E18.1.0.13"),sQuery(id+"F4.wireOp",EDGE,"E18.1.0.16"),sQuery(id+"F4.wireOp",EDGE,"E18.1.0.17"),sQuery(id+"F4.wireOp",EDGE,"E18.1.0.19"),sQuery(id+"F4.wireOp",EDGE,"E18.1.0.20")])],"isStart":false}),makeQuery(id+"F5.opExtrude","CAP_FACE",FACE,{"disambiguationData":[OSD([subQ1,subQ0,sQuery(id+"F4.wireOp",EDGE,"E18.2.0.0"),sQuery(id+"F4.wireOp",EDGE,"E18.2.0.2"),sQuery(id+"F4.wireOp",EDGE,"E18.2.0.3"),sQuery(id+"F4.wireOp",EDGE,"E18.2.0.4"),sQuery(id+"F4.wireOp",EDGE,"E18.2.0.5"),sQuery(id+"F4.wireOp",EDGE,"E18.2.0.8"),sQuery(id+"F4.wireOp",EDGE,"E18.2.0.10"),sQuery(id+"F4.wireOp",EDGE,"E18.2.0.14"),sQuery(id+"F4.wireOp",EDGE,"E18.2.0.15"),sQuery(id+"F4.wireOp",EDGE,"E18.2.0.18"),sQuery(id+"F4.wireOp",EDGE,"E18.2.0.21")])],"isStart":false}),makeQuery(id+"F5.opExtrude","CAP_FACE",FACE,{"disambiguationData":[OSD([subQ1,subQ0,sQuery(id+"F4.wireOp",EDGE,"E18.2.0.1"),sQuery(id+"F4.wireOp",EDGE,"E18.2.0.6"),sQuery(id+"F4.wireOp",EDGE,"E18.2.0.7"),sQuery(id+"F4.wireOp",EDGE,"E18.2.0.9"),sQuery(id+"F4.wireOp",EDGE,"E18.2.0.11"),sQuery(id+"F4.wireOp",EDGE,"E18.2.0.12"),sQuery(id+"F4.wireOp",EDGE,"E18.2.0.13"),sQuery(id+"F4.wireOp",EDGE,"E18.2.0.16"),sQuery(id+"F4.wireOp",EDGE,"E18.2.0.17"),sQuery(id+"F4.wireOp",EDGE,"E18.2.0.19"),sQuery(id+"F4.wireOp",EDGE,"E18.2.0.20")])],"isStart":false}),makeQuery(id+"F5.opExtrude","CAP_FACE",FACE,{"disambiguationData":[OSD([subQ1,subQ0,sQuery(id+"F4.wireOp",EDGE,"E19.1.0.0"),sQuery(id+"F4.wireOp",EDGE,"E19.1.0.1"),sQuery(id+"F4.wireOp",EDGE,"E19.1.0.2"),sQuery(id+"F4.wireOp",EDGE,"E19.1.0.3"),sQuery(id+"F4.wireOp",EDGE,"E19.1.0.4"),sQuery(id+"F4.wireOp",EDGE,"E19.1.0.5"),sQuery(id+"F4.wireOp",EDGE,"E19.1.0.6"),sQuery(id+"F4.wireOp",EDGE,"E19.1.0.7"),sQuery(id+"F4.wireOp",EDGE,"E19.1.0.8"),sQuery(id+"F4.wireOp",EDGE,"E19.1.0.9"),sQuery(id+"F4.wireOp",EDGE,"E19.1.0.10")])],"isStart":false})]});}
            var sketch = newSketch(context, id + "F11", { "sketchPlane" : qUnion([Q0])});
            skArc(sketch, "E31.0", {"start": v(187.83, 42.86) * mm, "mid": v(188.76, 45.1) * mm, "end": v(191, 46.04) * mm});
            skArc(sketch, "E31.1", {"start": v(181.48, 42.86) * mm, "mid": v(180.55, 45.1) * mm, "end": v(178.3, 46.04) * mm});
            skLineSegment(sketch, "E31.2", {"start": v(178.3, 47.85) * mm, "end": v(178.3, 46.04) * mm});
            skLineSegment(sketch, "E31.3", {"start": v(177.3, 46.04) * mm, "end": v(177.3, 47.85) * mm});
            skArc(sketch, "E31.4", {"start": v(174.12, 42.86) * mm, "mid": v(175.05, 45.1) * mm, "end": v(177.3, 46.04) * mm});
            skArc(sketch, "E31.5", {"start": v(167.77, 42.86) * mm, "mid": v(166.84, 45.1) * mm, "end": v(164.6, 46.04) * mm});
            skLineSegment(sketch, "E31.6", {"start": v(164.6, 47.85) * mm, "end": v(164.6, 46.04) * mm});
            skLineSegment(sketch, "E31.7", {"start": v(163.58, 46.04) * mm, "end": v(163.58, 47.85) * mm});
            skArc(sketch, "E31.8", {"start": v(160.4, 42.86) * mm, "mid": v(161.33, 45.1) * mm, "end": v(163.58, 46.04) * mm});
            skArc(sketch, "E31.9", {"start": v(154.05, 42.86) * mm, "mid": v(153.12, 45.1) * mm, "end": v(150.88, 46.04) * mm});
            skLineSegment(sketch, "E31.10", {"start": v(150.88, 47.85) * mm, "end": v(150.88, 46.04) * mm});
            skLineSegment(sketch, "E31.11", {"start": v(149.86, 46.04) * mm, "end": v(149.86, 47.85) * mm});
            skArc(sketch, "E31.12", {"start": v(146.69, 42.86) * mm, "mid": v(147.61, 45.1) * mm, "end": v(149.86, 46.04) * mm});
            skArc(sketch, "E31.13", {"start": v(140.34, 42.86) * mm, "mid": v(139.4, 45.1) * mm, "end": v(137.16, 46.04) * mm});
            skLineSegment(sketch, "E31.14", {"start": v(137.16, 47.85) * mm, "end": v(137.16, 46.04) * mm});
            skLineSegment(sketch, "E31.15", {"start": v(136.14, 46.04) * mm, "end": v(136.14, 47.85) * mm});
            skArc(sketch, "E31.16", {"start": v(132.97, 42.86) * mm, "mid": v(133.9, 45.1) * mm, "end": v(136.14, 46.04) * mm});
            skLineSegment(sketch, "E31.17", {"start": v(123.44, 47.85) * mm, "end": v(123.44, 46.04) * mm});
            skLineSegment(sketch, "E31.18", {"start": v(122.43, 46.04) * mm, "end": v(122.43, 47.85) * mm});
            skArc(sketch, "E31.19", {"start": v(119.25, 42.86) * mm, "mid": v(120.18, 45.1) * mm, "end": v(122.43, 46.04) * mm});
            skArc(sketch, "E31.20", {"start": v(126.62, 42.86) * mm, "mid": v(125.69, 45.1) * mm, "end": v(123.44, 46.04) * mm});
            skArc(sketch, "E31.21", {"start": v(112.9, 42.86) * mm, "mid": v(111.97, 45.1) * mm, "end": v(109.73, 46.04) * mm});
            skArc(sketch, "E31.22", {"start": v(105.54, 42.86) * mm, "mid": v(106.47, 45.1) * mm, "end": v(108.71, 46.04) * mm});
            skLineSegment(sketch, "E31.23", {"start": v(108.71, 46.04) * mm, "end": v(108.71, 47.85) * mm});
            skLineSegment(sketch, "E31.24", {"start": v(109.73, 47.85) * mm, "end": v(109.73, 46.04) * mm});
            skArc(sketch, "E31.25", {"start": v(99.19, 42.86) * mm, "mid": v(98.26, 45.1) * mm, "end": v(96.01, 46.04) * mm});
            skLineSegment(sketch, "E31.26", {"start": v(96.01, 47.85) * mm, "end": v(96.01, 46.04) * mm});
            skLineSegment(sketch, "E31.27", {"start": v(95, 46.04) * mm, "end": v(95, 47.85) * mm});
            skArc(sketch, "E31.28", {"start": v(91.82, 42.86) * mm, "mid": v(92.75, 45.1) * mm, "end": v(95, 46.04) * mm});
            skArc(sketch, "E31.29", {"start": v(85.47, 42.86) * mm, "mid": v(84.54, 45.1) * mm, "end": v(82.3, 46.04) * mm});
            skLineSegment(sketch, "E31.30", {"start": v(82.3, 47.85) * mm, "end": v(82.3, 46.04) * mm});
            skLineSegment(sketch, "E31.31", {"start": v(81.28, 46.04) * mm, "end": v(81.28, 47.85) * mm});
            skArc(sketch, "E31.32", {"start": v(78.1, 42.86) * mm, "mid": v(79.03, 45.1) * mm, "end": v(81.28, 46.04) * mm});
            skArc(sketch, "E31.33", {"start": v(71.76, 42.86) * mm, "mid": v(70.83, 45.1) * mm, "end": v(68.58, 46.04) * mm});
            skLineSegment(sketch, "E31.34", {"start": v(68.58, 47.85) * mm, "end": v(68.58, 46.04) * mm});
            skLineSegment(sketch, "E31.35", {"start": v(67.56, 46.04) * mm, "end": v(67.56, 47.85) * mm});
            skArc(sketch, "E31.36", {"start": v(64.39, 42.86) * mm, "mid": v(65.32, 45.1) * mm, "end": v(67.56, 46.04) * mm});
            skArc(sketch, "E31.37", {"start": v(58.04, 42.86) * mm, "mid": v(57.1, 45.1) * mm, "end": v(54.86, 46.04) * mm});
            skLineSegment(sketch, "E31.38", {"start": v(54.86, 47.85) * mm, "end": v(54.86, 46.04) * mm});
            skLineSegment(sketch, "E31.39", {"start": v(53.85, 46.04) * mm, "end": v(53.85, 47.85) * mm});
            skArc(sketch, "E31.40", {"start": v(50.67, 42.86) * mm, "mid": v(51.6, 45.1) * mm, "end": v(53.85, 46.04) * mm});
            skArc(sketch, "E31.41", {"start": v(44.32, 42.86) * mm, "mid": v(43.4, 45.1) * mm, "end": v(41.15, 46.04) * mm});
            skLineSegment(sketch, "E31.42", {"start": v(41.15, 47.85) * mm, "end": v(41.15, 46.04) * mm});
            skLineSegment(sketch, "E31.43", {"start": v(40.13, 46.04) * mm, "end": v(40.13, 47.85) * mm});
            skArc(sketch, "E31.44", {"start": v(36.96, 42.86) * mm, "mid": v(37.89, 45.1) * mm, "end": v(40.13, 46.04) * mm});
            skArc(sketch, "E31.45", {"start": v(30.6, 42.86) * mm, "mid": v(29.68, 45.1) * mm, "end": v(27.43, 46.04) * mm});
            skLineSegment(sketch, "E31.46", {"start": v(27.43, 47.85) * mm, "end": v(27.43, 46.04) * mm});
            skLineSegment(sketch, "E31.47", {"start": v(26.42, 46.04) * mm, "end": v(26.42, 47.85) * mm});
            skArc(sketch, "E31.48", {"start": v(23.24, 42.86) * mm, "mid": v(24.17, 45.1) * mm, "end": v(26.42, 46.04) * mm});
            skArc(sketch, "E31.49", {"start": v(16.9, 42.86) * mm, "mid": v(15.96, 45.1) * mm, "end": v(13.72, 46.04) * mm});
            skLineSegment(sketch, "E31.50", {"start": v(13.72, 47.85) * mm, "end": v(13.72, 46.04) * mm});
            skLineSegment(sketch, "E31.51", {"start": v(12.7, 46.04) * mm, "end": v(12.7, 47.85) * mm});
            skLineSegment(sketch, "E32", {"start": v(64.39, 42.86) * mm, "end": v(71.76, 42.86) * mm});
            skLineSegment(sketch, "E33", {"start": v(67.56, 47.85) * mm, "end": v(68.58, 47.85) * mm});
            skLineSegment(sketch, "E34", {"start": v(78.1, 42.86) * mm, "end": v(85.47, 42.86) * mm});
            skLineSegment(sketch, "E35", {"start": v(81.28, 47.85) * mm, "end": v(82.3, 47.85) * mm});
            skLineSegment(sketch, "E36", {"start": v(13.72, 47.85) * mm, "end": v(12.7, 47.85) * mm});
            skLineSegment(sketch, "E37", {"start": v(12.7, 46.04) * mm, "end": v(12.7, 42.86) * mm});
            skLineSegment(sketch, "E38", {"start": v(12.7, 42.86) * mm, "end": v(16.9, 42.86) * mm});
            skLineSegment(sketch, "E39", {"start": v(23.24, 42.86) * mm, "end": v(30.6, 42.86) * mm});
            skLineSegment(sketch, "E40", {"start": v(26.42, 47.85) * mm, "end": v(27.43, 47.85) * mm});
            skLineSegment(sketch, "E41", {"start": v(36.96, 42.86) * mm, "end": v(44.32, 42.86) * mm});
            skLineSegment(sketch, "E42", {"start": v(40.13, 47.85) * mm, "end": v(41.15, 47.85) * mm});
            skLineSegment(sketch, "E43", {"start": v(50.67, 42.86) * mm, "end": v(58.04, 42.86) * mm});
            skLineSegment(sketch, "E44", {"start": v(53.85, 47.85) * mm, "end": v(54.86, 47.85) * mm});
            skLineSegment(sketch, "E45", {"start": v(91.82, 42.86) * mm, "end": v(99.19, 42.86) * mm});
            skLineSegment(sketch, "E46", {"start": v(95, 47.85) * mm, "end": v(96.01, 47.85) * mm});
            skLineSegment(sketch, "E47", {"start": v(108.71, 47.85) * mm, "end": v(109.73, 47.85) * mm});
            skLineSegment(sketch, "E48", {"start": v(105.54, 42.86) * mm, "end": v(112.9, 42.86) * mm});
            skLineSegment(sketch, "E49", {"start": v(122.43, 47.85) * mm, "end": v(123.44, 47.85) * mm});
            skLineSegment(sketch, "E50", {"start": v(119.25, 42.86) * mm, "end": v(126.62, 42.86) * mm});
            skLineSegment(sketch, "E51", {"start": v(191, 46.04) * mm, "end": v(191, 42.86) * mm});
            skLineSegment(sketch, "E52", {"start": v(191, 42.86) * mm, "end": v(187.83, 42.86) * mm});
            skLineSegment(sketch, "E53", {"start": v(177.3, 47.85) * mm, "end": v(178.3, 47.85) * mm});
            skLineSegment(sketch, "E54", {"start": v(174.12, 42.86) * mm, "end": v(181.48, 42.86) * mm});
            skLineSegment(sketch, "E55", {"start": v(163.58, 47.85) * mm, "end": v(164.6, 47.85) * mm});
            skLineSegment(sketch, "E56", {"start": v(160.4, 42.86) * mm, "end": v(167.77, 42.86) * mm});
            skLineSegment(sketch, "E57", {"start": v(149.86, 47.85) * mm, "end": v(150.88, 47.85) * mm});
            skLineSegment(sketch, "E58", {"start": v(146.69, 42.86) * mm, "end": v(154.05, 42.86) * mm});
            skLineSegment(sketch, "E59", {"start": v(136.14, 47.85) * mm, "end": v(137.16, 47.85) * mm});
            skLineSegment(sketch, "E60", {"start": v(132.97, 42.86) * mm, "end": v(140.34, 42.86) * mm});
            skSolve(sketch);
        }
        {
            var Q0;
            Q0 = qSketchRegion(id + "F11", true);
            var Q1;
            Q1=makeQuery(id+"F11.imprint","IMPRINT",FACE,{"disambiguationData":[TD([[makeQuery(id+"F11.imprint","IMPRINT",EDGE,{"derivedFrom":sQuery(id+"F11.wireOp",EDGE,"E31.0")}),-1.0]])]});
            var Q2;
            Q2=makeQuery(id+"F11.imprint","IMPRINT",FACE,{"disambiguationData":[TD([[makeQuery(id+"F11.imprint","IMPRINT",EDGE,{"derivedFrom":sQuery(id+"F11.wireOp",EDGE,"E31.1")}),1.0]])]});
            var Q3;
            Q3=makeQuery(id+"F11.imprint","IMPRINT",FACE,{"disambiguationData":[TD([[makeQuery(id+"F11.imprint","IMPRINT",EDGE,{"derivedFrom":sQuery(id+"F11.wireOp",EDGE,"E31.5")}),1.0]])]});
            var Q4;
            Q4=makeQuery(id+"F11.imprint","IMPRINT",FACE,{"disambiguationData":[TD([[makeQuery(id+"F11.imprint","IMPRINT",EDGE,{"derivedFrom":sQuery(id+"F11.wireOp",EDGE,"E31.9")}),1.0]])]});
            var Q5;
            Q5=makeQuery(id+"F11.imprint","IMPRINT",FACE,{"disambiguationData":[TD([[makeQuery(id+"F11.imprint","IMPRINT",EDGE,{"derivedFrom":sQuery(id+"F11.wireOp",EDGE,"E31.13")}),1.0]])]});
            extrude(context, id + "F12", {"entities" : qUnion([Q0, Q1, Q2, Q3, Q4, Q5]), "operationType" : NewBodyOperationType.REMOVE, "endBound" : BoundingType.THROUGH_ALL, "oppositeDirection" : true, "depth" : 25.4 * mm});
        }
        {
            var Q0;
            Q0=makeQuery(id+"F1.opExtrude","SWEPT_BODY",BODY,{"disambiguationData":[OSD([sQuery(id+"F0.wireOp",EDGE,"E0.bottom"),sQuery(id+"F0.wireOp",EDGE,"E0.top"),sQuery(id+"F0.wireOp",EDGE,"E0.left"),sQuery(id+"F0.wireOp",EDGE,"E0.right")])]});
            var Q1;
            Q1=qCreatedBy(makeId("Front.planeOp"),FACE);
            mirror(context, id + "F13", {"operationType" : NewBodyOperationType.ADD, "entities" : qUnion([Q0]), "mirrorPlane" : qUnion([Q1])});
        }
    });
